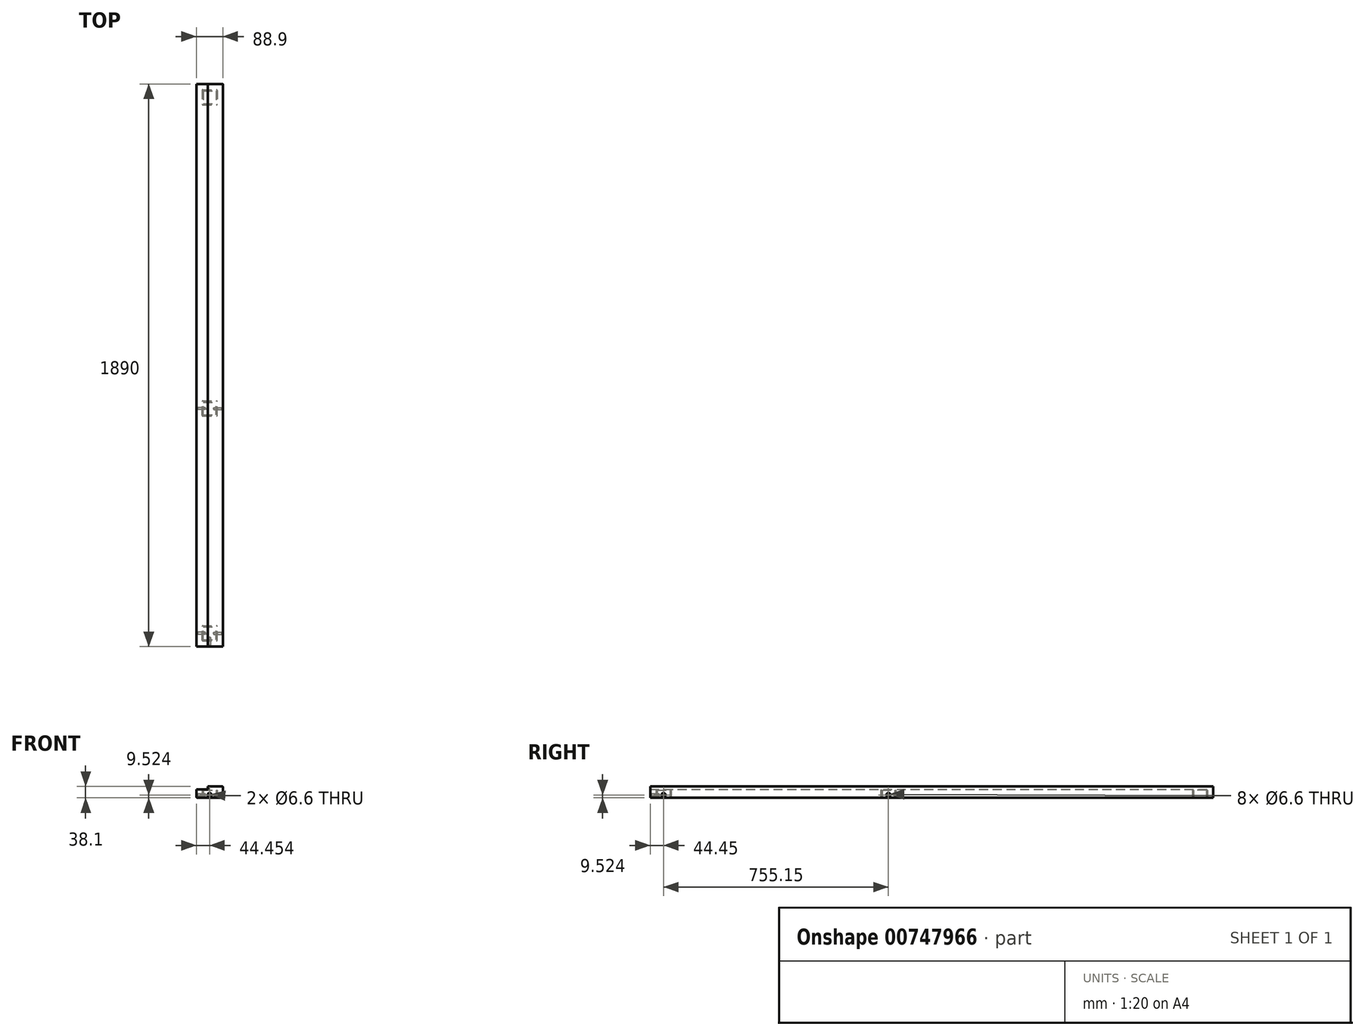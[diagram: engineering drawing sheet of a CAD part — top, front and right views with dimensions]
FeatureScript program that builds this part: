
annotation { "Feature Type Name" : "Feature", "Feature Type Description" : "" }
export const myFeature = defineFeature(function(context is Context, id is Id, definition is map)
    precondition{}
    {
        {
            var Q0;
            Q0=qCreatedBy(makeId("Front.planeOp"),FACE);
            var sketch = newSketch(context, id + "F0", { "sketchPlane" : qUnion([Q0])});
            skLineSegment(sketch, "E0.bottom", {"start": v(-21.3, 49.02) * mm, "end": v(26.5, 49.02) * mm});
            skLineSegment(sketch, "E0.top", {"start": v(-56.4, 10.92) * mm, "end": v(26.5, 10.92) * mm});
            skLineSegment(sketch, "E0.left", {"start": v(-59.4, 39.5) * mm, "end": v(-59.4, 13.92) * mm});
            skLineSegment(sketch, "E0.right", {"start": v(29.5, 46.02) * mm, "end": v(29.5, 13.92) * mm});
            skPoint(sketch, "E1.visualSharp", {"position": v(-59.4, 49.02) * mm});
            skPoint(sketch, "E2.visualSharp", {"position": v(-59.4, 10.92) * mm});
            skArc(sketch, "E2.filletArc", {"start": v(-59.4, 13.92) * mm, "mid": v(-58.52, 11.8) * mm, "end": v(-56.4, 10.92) * mm});
            skPoint(sketch, "E3.visualSharp", {"position": v(29.5, 49.02) * mm});
            skArc(sketch, "E3.filletArc", {"start": v(29.5, 46.02) * mm, "mid": v(28.63, 48.14) * mm, "end": v(26.5, 49.02) * mm});
            skPoint(sketch, "E4.visualSharp", {"position": v(29.5, 10.92) * mm});
            skArc(sketch, "E4.filletArc", {"start": v(26.5, 10.92) * mm, "mid": v(28.63, 11.8) * mm, "end": v(29.5, 13.92) * mm});
            skLineSegment(sketch, "E5", {"start": v(-21.3, 49.02) * mm, "end": v(-21.3, 39.5) * mm});
            skLineSegment(sketch, "E6", {"start": v(-21.3, 39.5) * mm, "end": v(-59.4, 39.5) * mm});
            skSolve(sketch);
        }
        {
            var Q0;
            Q0=makeQuery(id+"F0.imprint","IMPRINT",FACE,{"disambiguationData":[TD([[makeQuery(id+"F0.imprint","IMPRINT",EDGE,{"derivedFrom":sQuery(id+"F0.wireOp",EDGE,"E0.bottom")}),-1.0]])]});
            extrude(context, id + "F1", {"entities" : qUnion([Q0]), "depth" : 1890 * mm, "offsetDistance" : 25 * mm});
        }
        {
            var Q0;
            Q0=makeQuery(id+"F1.opExtrude","SWEPT_EDGE",EDGE,{"disambiguationData":[OSD([sQuery(id+"F0.wireOp",EDGE,"E0.bottom"),sQuery(id+"F0.wireOp",EDGE,"E3.filletArc")])]});
            cPoint(context, id + "F2", {"entities" : qUnion([Q0]), "parameter" : 0.5});
        }
        {
            var Q0;
            Q0=makeQuery(id+"F1.opExtrude","SWEPT_EDGE",EDGE,{"disambiguationData":[OSD([sQuery(id+"F0.wireOp",EDGE,"E0.left"),sQuery(id+"F0.wireOp",EDGE,"E2.filletArc")])]});
            cPoint(context, id + "F3", {"entities" : qUnion([Q0]), "parameter" : 0.5});
        }
        {
            var Q0;
            Q0=makeQuery(id+"F1.opExtrude","SWEPT_EDGE",EDGE,{"disambiguationData":[OSD([sQuery(id+"F0.wireOp",EDGE,"E5"),sQuery(id+"F0.wireOp",EDGE,"E6")])]});
            cPoint(context, id + "F4", {"entities" : qUnion([Q0]), "parameter" : 0.5});
        }
        {
            var Q0;
            Q0 = qCreatedBy(id + "F2" ,VERTEX);
            var Q1;
            Q1 = qCreatedBy(id + "F3" ,VERTEX);
            var Q2;
            Q2 = qCreatedBy(id + "F4" ,VERTEX);
            cPlane(context, id + "F5", {"entities" : qUnion([Q0, Q1, Q2]), "cplaneType" : CPlaneType.THREE_POINT, "offset" : 25 * mm, "width" : 150 * mm, "height" : 150 * mm});
        }
        {
            var Q0;
            Q0=makeQuery(id+"F1.opExtrude","SWEPT_FACE",FACE,{"disambiguationData":[OSD([sQuery(id+"F0.wireOp",EDGE,"E0.top")])]});
            var sketch = newSketch(context, id + "F6", { "sketchPlane" : qUnion([Q0])});
            skLineSegment(sketch, "E7.bottom", {"start": v(-37.85, 1870.95) * mm, "end": v(7.95, 1870.95) * mm});
            skLineSegment(sketch, "E7.top", {"start": v(-37.85, 1820.15) * mm, "end": v(7.95, 1820.15) * mm});
            skLineSegment(sketch, "E7.left", {"start": v(-40.35, 1868.45) * mm, "end": v(-40.35, 1822.65) * mm});
            skLineSegment(sketch, "E7.right", {"start": v(10.45, 1868.45) * mm, "end": v(10.45, 1822.65) * mm});
            skPoint(sketch, "E8.visualSharp", {"position": v(-40.35, 1870.95) * mm});
            skArc(sketch, "E8.filletArc", {"start": v(-37.85, 1870.95) * mm, "mid": v(-39.61, 1870.22) * mm, "end": v(-40.35, 1868.45) * mm});
            skPoint(sketch, "E9.visualSharp", {"position": v(-40.35, 1820.15) * mm});
            skArc(sketch, "E9.filletArc", {"start": v(-40.35, 1822.65) * mm, "mid": v(-39.61, 1820.88) * mm, "end": v(-37.85, 1820.15) * mm});
            skPoint(sketch, "E10.visualSharp", {"position": v(10.45, 1820.15) * mm});
            skArc(sketch, "E10.filletArc", {"start": v(7.95, 1820.15) * mm, "mid": v(9.72, 1820.88) * mm, "end": v(10.45, 1822.65) * mm});
            skPoint(sketch, "E11.visualSharp", {"position": v(10.45, 1870.95) * mm});
            skArc(sketch, "E11.filletArc", {"start": v(10.45, 1868.45) * mm, "mid": v(9.72, 1870.22) * mm, "end": v(7.95, 1870.95) * mm});
            skLineSegment(sketch, "E12.1", {"start": v(-36.35, 1866.95) * mm, "end": v(-36.35, 1824.15) * mm});
            skLineSegment(sketch, "E12.2", {"start": v(-36.35, 1866.95) * mm, "end": v(6.45, 1866.95) * mm});
            skLineSegment(sketch, "E12.5", {"start": v(6.45, 1866.95) * mm, "end": v(6.45, 1824.15) * mm});
            skLineSegment(sketch, "E12.7", {"start": v(-36.35, 1824.15) * mm, "end": v(6.45, 1824.15) * mm});
            skLineSegment(sketch, "E13", {"start": v(10.45, 1870.95) * mm, "end": v(-40.35, 1820.15) * mm, "construction": true});
            skLineSegment(sketch, "E14.0", {"start": v(-56.4, 1890) * mm, "end": v(26.5, 1890) * mm});
            skPoint(sketch, "E15", {"position": v(-14.95, 1845.55) * mm});
            skPoint(sketch, "E16", {"position": v(-14.95, 1890) * mm});
            skLineSegment(sketch, "E17", {"start": v(-56.4, 945) * mm, "end": v(26.5, 945) * mm, "construction": true});
            skLineSegment(sketch, "E18.bottom", {"start": v(-37.85, 1115.8) * mm, "end": v(7.95, 1115.8) * mm});
            skLineSegment(sketch, "E18.top", {"start": v(-37.85, 1065) * mm, "end": v(7.95, 1065) * mm});
            skLineSegment(sketch, "E18.left", {"start": v(-40.35, 1113.3) * mm, "end": v(-40.35, 1067.5) * mm});
            skLineSegment(sketch, "E18.right", {"start": v(10.45, 1113.3) * mm, "end": v(10.45, 1067.5) * mm});
            skPoint(sketch, "E19.visualSharp", {"position": v(-40.35, 1115.8) * mm});
            skArc(sketch, "E19.filletArc", {"start": v(-37.85, 1115.8) * mm, "mid": v(-39.61, 1115.07) * mm, "end": v(-40.35, 1113.3) * mm});
            skPoint(sketch, "E20.visualSharp", {"position": v(-40.35, 1065) * mm});
            skArc(sketch, "E20.filletArc", {"start": v(-40.35, 1067.5) * mm, "mid": v(-39.61, 1065.73) * mm, "end": v(-37.85, 1065) * mm});
            skPoint(sketch, "E21.visualSharp", {"position": v(10.45, 1065) * mm});
            skArc(sketch, "E21.filletArc", {"start": v(7.95, 1065) * mm, "mid": v(9.72, 1065.73) * mm, "end": v(10.45, 1067.5) * mm});
            skPoint(sketch, "E22.visualSharp", {"position": v(10.45, 1115.8) * mm});
            skArc(sketch, "E22.filletArc", {"start": v(10.45, 1113.3) * mm, "mid": v(9.72, 1115.07) * mm, "end": v(7.95, 1115.8) * mm});
            skLineSegment(sketch, "E23.1", {"start": v(-36.35, 1111.8) * mm, "end": v(-36.35, 1069) * mm});
            skLineSegment(sketch, "E23.2", {"start": v(-36.35, 1111.8) * mm, "end": v(6.45, 1111.8) * mm});
            skLineSegment(sketch, "E23.5", {"start": v(6.45, 1111.8) * mm, "end": v(6.45, 1069) * mm});
            skLineSegment(sketch, "E23.7", {"start": v(-36.35, 1069) * mm, "end": v(6.45, 1069) * mm});
            skLineSegment(sketch, "E24", {"start": v(10.45, 1115.8) * mm, "end": v(-40.35, 1065) * mm, "construction": true});
            skPoint(sketch, "E25", {"position": v(-14.95, 1090.4) * mm});
            skPoint(sketch, "E26", {"position": v(-14.95, 945) * mm});
            skLineSegment(sketch, "E27.MirrorCS", {"start": v(-36.35, 23.05) * mm, "end": v(-36.35, 65.85) * mm});
            skArc(sketch, "E28.MirrorCS", {"start": v(7.95, 69.85) * mm, "mid": v(9.72, 69.12) * mm, "end": v(10.45, 67.35) * mm});
            skArc(sketch, "E29.MirrorCS", {"start": v(10.45, 21.55) * mm, "mid": v(9.72, 19.78) * mm, "end": v(7.95, 19.05) * mm});
            skArc(sketch, "E30.MirrorCS", {"start": v(-37.85, 19.05) * mm, "mid": v(-39.61, 19.78) * mm, "end": v(-40.35, 21.55) * mm});
            skLineSegment(sketch, "E31.MirrorCS", {"start": v(-36.35, 23.05) * mm, "end": v(6.45, 23.05) * mm});
            skLineSegment(sketch, "E32.MirrorCS", {"start": v(-36.35, 65.85) * mm, "end": v(6.45, 65.85) * mm});
            skLineSegment(sketch, "E33.MirrorCS", {"start": v(-37.85, 69.85) * mm, "end": v(7.95, 69.85) * mm});
            skLineSegment(sketch, "E34.MirrorCS", {"start": v(6.45, 23.05) * mm, "end": v(6.45, 65.85) * mm});
            skLineSegment(sketch, "E35.MirrorCS", {"start": v(-40.35, 21.55) * mm, "end": v(-40.35, 67.35) * mm});
            skLineSegment(sketch, "E36.MirrorCS", {"start": v(-56.4, 0) * mm, "end": v(26.5, 0) * mm});
            skArc(sketch, "E37.MirrorCS", {"start": v(-40.35, 67.35) * mm, "mid": v(-39.61, 69.12) * mm, "end": v(-37.85, 69.85) * mm});
            skLineSegment(sketch, "E38.MirrorCS", {"start": v(-37.85, 19.05) * mm, "end": v(7.95, 19.05) * mm});
            skLineSegment(sketch, "E39.MirrorCS", {"start": v(10.45, 21.55) * mm, "end": v(10.45, 67.35) * mm});
            skLineSegment(sketch, "E40.MirrorCS", {"start": v(10.45, 19.05) * mm, "end": v(-40.35, 69.85) * mm, "construction": true});
            skPoint(sketch, "E41.MirrorP", {"position": v(-14.95, 44.45) * mm});
            skPoint(sketch, "E42.MirrorP", {"position": v(-14.95, 0) * mm});
            skPoint(sketch, "E43.MirrorP", {"position": v(-40.35, 19.05) * mm});
            skPoint(sketch, "E44.MirrorP", {"position": v(-40.35, 69.85) * mm});
            skPoint(sketch, "E45.MirrorP", {"position": v(10.45, 19.05) * mm});
            skPoint(sketch, "E46.MirrorP", {"position": v(10.45, 69.85) * mm});
            skSolve(sketch);
        }
        {
            var Q0;
            Q0 = qSketchRegion(id + "F6", true);
            extrude(context, id + "F7", {"entities" : qUnion([Q0]), "operationType" : NewBodyOperationType.REMOVE, "oppositeDirection" : true, "depth" : 25 * mm - 3 / 203.2 * mm, "offsetDistance" : 25 * mm});
        }
        {
            var Q0;
            Q0=makeQuery(id+"F1.opExtrude","CAP_FACE",FACE,{"disambiguationData":[OSD([sQuery(id+"F0.wireOp",EDGE,"E0.bottom"),sQuery(id+"F0.wireOp",EDGE,"E0.top"),sQuery(id+"F0.wireOp",EDGE,"E0.left"),sQuery(id+"F0.wireOp",EDGE,"E0.right"),sQuery(id+"F0.wireOp",EDGE,"E2.filletArc"),sQuery(id+"F0.wireOp",EDGE,"E3.filletArc"),sQuery(id+"F0.wireOp",EDGE,"E4.filletArc"),sQuery(id+"F0.wireOp",EDGE,"E5"),sQuery(id+"F0.wireOp",EDGE,"E6")])],"isStart":false});
            var sketch = newSketch(context, id + "F8", { "sketchPlane" : qUnion([Q0])});
            skLineSegment(sketch, "E47.0", {"start": v(-37.85, 26.4) * mm, "end": v(7.95, 26.4) * mm, "construction": true});
            skPoint(sketch, "E48", {"position": v(-14.95, 26.4) * mm});
            skPoint(sketch, "E49", {"position": v(-14.95, 20.44) * mm});
            skSolve(sketch);
        }
        {
            var Q0;
            Q0=sQuery(id+"F8.wireOp",VERTEX,"E49");
            var Q1;
            Q1=makeQuery(id+"F1.opExtrude","SWEPT_BODY",BODY,{"disambiguationData":[OSD([sQuery(id+"F0.wireOp",EDGE,"E0.bottom"),sQuery(id+"F0.wireOp",EDGE,"E0.top"),sQuery(id+"F0.wireOp",EDGE,"E0.left"),sQuery(id+"F0.wireOp",EDGE,"E0.right"),sQuery(id+"F0.wireOp",EDGE,"E2.filletArc"),sQuery(id+"F0.wireOp",EDGE,"E3.filletArc"),sQuery(id+"F0.wireOp",EDGE,"E4.filletArc"),sQuery(id+"F0.wireOp",EDGE,"E5"),sQuery(id+"F0.wireOp",EDGE,"E6")])]});
            hole(context, id + "F9", {"style" : HoleStyle.C_SINK, "endStyle" : HoleEndStyle.BLIND, "standardTappedOrClearance" : lookupTablePath({ "fit" : "Normal", "standard" : "ISO", "size" : "M6", "type" : "Clearance" }), "standardBlindInLast" : lookupTablePath({ "fit" : "Standard", "standard" : "ISO", "size" : "M6", "type" : "Clearance" }), "holeDiameter" : 6.6 * mm, "cSinkDiameter" : 13.44 * mm, "cSinkAngle" : 90 * degree, "majorDiameter" : 6 * mm, "holeDepth" : 30 * mm, "isTappedThrough" : true, "tappedDepth" : 12 * mm, "tapClearance" : 3, "startFromSketch" : true, "locations" : qUnion([Q0]), "scope" : qUnion([Q1])});
        }
        {
            var Q0;
            Q0=makeQuery(id+"F1.opExtrude","SWEPT_FACE",FACE,{"disambiguationData":[OSD([sQuery(id+"F0.wireOp",EDGE,"E0.right")])]});
            var sketch = newSketch(context, id + "F10", { "sketchPlane" : qUnion([Q0])});
            skLineSegment(sketch, "E50.0", {"start": v(-1868.45, 26.4) * mm, "end": v(-1822.65, 26.4) * mm, "construction": true});
            skPoint(sketch, "E51", {"position": v(-1845.55, 20.44) * mm});
            skPoint(sketch, "E51.positionSnap0", {"position": v(-1845.55, 26.4) * mm});
            skLineSegment(sketch, "E52.0", {"start": v(-1113.3, 26.4) * mm, "end": v(-1067.5, 26.4) * mm, "construction": true});
            skPoint(sketch, "E53", {"position": v(-1090.4, 20.44) * mm});
            skPoint(sketch, "E53.positionSnap0", {"position": v(-1090.4, 26.4) * mm});
            skSolve(sketch);
        }
        {
            var Q0;
            Q0=sQuery(id+"F10.wireOp",VERTEX,"E51");
            var Q1;
            Q1=makeQuery(id+"F1.opExtrude","SWEPT_BODY",BODY,{"disambiguationData":[OSD([sQuery(id+"F0.wireOp",EDGE,"E0.bottom"),sQuery(id+"F0.wireOp",EDGE,"E0.top"),sQuery(id+"F0.wireOp",EDGE,"E0.left"),sQuery(id+"F0.wireOp",EDGE,"E0.right"),sQuery(id+"F0.wireOp",EDGE,"E2.filletArc"),sQuery(id+"F0.wireOp",EDGE,"E3.filletArc"),sQuery(id+"F0.wireOp",EDGE,"E4.filletArc"),sQuery(id+"F0.wireOp",EDGE,"E5"),sQuery(id+"F0.wireOp",EDGE,"E6")])]});
            hole(context, id + "F11", {"style" : HoleStyle.C_SINK, "endStyle" : HoleEndStyle.BLIND, "standardTappedOrClearance" : lookupTablePath({ "fit" : "Normal", "standard" : "ISO", "size" : "M6", "type" : "Clearance" }), "standardBlindInLast" : lookupTablePath({ "fit" : "Standard", "standard" : "ISO", "size" : "M6", "type" : "Clearance" }), "holeDiameter" : 6.6 * mm, "cSinkDiameter" : 13.44 * mm, "cSinkAngle" : 90 * degree, "majorDiameter" : 6 * mm, "holeDepth" : 30 * mm, "isTappedThrough" : true, "tappedDepth" : 27 * mm, "tapClearance" : 3, "startFromSketch" : true, "locations" : qUnion([Q0]), "scope" : qUnion([Q1])});
        }
        {
            var Q0;
            Q0=makeQuery(id+"F1.opExtrude","SWEPT_FACE",FACE,{"disambiguationData":[OSD([sQuery(id+"F0.wireOp",EDGE,"E0.left")])]});
            var sketch = newSketch(context, id + "F12", { "sketchPlane" : qUnion([Q0])});
            skLineSegment(sketch, "E54.0", {"start": v(1868.45, 26.4) * mm, "end": v(1822.65, 26.4) * mm, "construction": true});
            skPoint(sketch, "E55", {"position": v(1845.55, 20.44) * mm});
            skPoint(sketch, "E55.positionSnap0", {"position": v(1845.55, 26.4) * mm});
            skLineSegment(sketch, "E56.0", {"start": v(1113.3, 26.4) * mm, "end": v(1067.5, 26.4) * mm, "construction": true});
            skPoint(sketch, "E57", {"position": v(1090.4, 20.44) * mm});
            skPoint(sketch, "E57.positionSnap0", {"position": v(1090.4, 26.4) * mm});
            skSolve(sketch);
        }
        {
            var Q0;
            Q0=sQuery(id+"F12.wireOp",VERTEX,"E55");
            var Q1;
            Q1=makeQuery(id+"F1.opExtrude","SWEPT_BODY",BODY,{"disambiguationData":[OSD([sQuery(id+"F0.wireOp",EDGE,"E0.bottom"),sQuery(id+"F0.wireOp",EDGE,"E0.top"),sQuery(id+"F0.wireOp",EDGE,"E0.left"),sQuery(id+"F0.wireOp",EDGE,"E0.right"),sQuery(id+"F0.wireOp",EDGE,"E2.filletArc"),sQuery(id+"F0.wireOp",EDGE,"E3.filletArc"),sQuery(id+"F0.wireOp",EDGE,"E4.filletArc"),sQuery(id+"F0.wireOp",EDGE,"E5"),sQuery(id+"F0.wireOp",EDGE,"E6")])]});
            hole(context, id + "F13", {"style" : HoleStyle.C_SINK, "endStyle" : HoleEndStyle.BLIND, "standardTappedOrClearance" : lookupTablePath({ "fit" : "Normal", "standard" : "ISO", "size" : "M6", "type" : "Clearance" }), "standardBlindInLast" : lookupTablePath({ "fit" : "Standard", "standard" : "ISO", "size" : "M6", "type" : "Clearance" }), "holeDiameter" : 6.6 * mm, "cSinkDiameter" : 13.44 * mm, "cSinkAngle" : 90 * degree, "majorDiameter" : 5 * mm, "holeDepth" : 30 * mm, "isTappedThrough" : true, "tappedDepth" : 12 * mm, "tapClearance" : 3, "startFromSketch" : true, "locations" : qUnion([Q0]), "scope" : qUnion([Q1])});
        }
        {
            var Q0;
            Q0=sQuery(id+"F12.wireOp",VERTEX,"E57");
            var Q1;
            Q1=makeQuery(id+"F1.opExtrude","SWEPT_BODY",BODY,{"disambiguationData":[OSD([sQuery(id+"F0.wireOp",EDGE,"E0.bottom"),sQuery(id+"F0.wireOp",EDGE,"E0.top"),sQuery(id+"F0.wireOp",EDGE,"E0.left"),sQuery(id+"F0.wireOp",EDGE,"E0.right"),sQuery(id+"F0.wireOp",EDGE,"E2.filletArc"),sQuery(id+"F0.wireOp",EDGE,"E3.filletArc"),sQuery(id+"F0.wireOp",EDGE,"E4.filletArc"),sQuery(id+"F0.wireOp",EDGE,"E5"),sQuery(id+"F0.wireOp",EDGE,"E6")])]});
            hole(context, id + "F14", {"style" : HoleStyle.C_SINK, "endStyle" : HoleEndStyle.BLIND, "standardTappedOrClearance" : lookupTablePath({ "fit" : "Normal", "standard" : "ISO", "size" : "M6", "type" : "Clearance" }), "standardBlindInLast" : lookupTablePath({ "fit" : "Standard", "standard" : "ISO", "size" : "M6", "type" : "Clearance" }), "holeDiameter" : 6.6 * mm, "cSinkDiameter" : 13.44 * mm, "cSinkAngle" : 90 * degree, "majorDiameter" : 5 * mm, "holeDepth" : 30 * mm, "isTappedThrough" : true, "tappedDepth" : 12 * mm, "tapClearance" : 3, "startFromSketch" : true, "locations" : qUnion([Q0]), "scope" : qUnion([Q1])});
        }
        {
            var Q0;
            Q0=sQuery(id+"F10.wireOp",VERTEX,"E53");
            var Q1;
            Q1=makeQuery(id+"F1.opExtrude","SWEPT_BODY",BODY,{"disambiguationData":[OSD([sQuery(id+"F0.wireOp",EDGE,"E0.bottom"),sQuery(id+"F0.wireOp",EDGE,"E0.top"),sQuery(id+"F0.wireOp",EDGE,"E0.left"),sQuery(id+"F0.wireOp",EDGE,"E0.right"),sQuery(id+"F0.wireOp",EDGE,"E2.filletArc"),sQuery(id+"F0.wireOp",EDGE,"E3.filletArc"),sQuery(id+"F0.wireOp",EDGE,"E4.filletArc"),sQuery(id+"F0.wireOp",EDGE,"E5"),sQuery(id+"F0.wireOp",EDGE,"E6")])]});
            hole(context, id + "F15", {"style" : HoleStyle.C_SINK, "endStyle" : HoleEndStyle.BLIND, "standardTappedOrClearance" : lookupTablePath({ "fit" : "Normal", "standard" : "ISO", "size" : "M6", "type" : "Clearance" }), "standardBlindInLast" : lookupTablePath({ "fit" : "Standard", "standard" : "ISO", "size" : "M6", "type" : "Clearance" }), "holeDiameter" : 6.6 * mm, "cSinkDiameter" : 13.44 * mm, "cSinkAngle" : 90 * degree, "majorDiameter" : 5 * mm, "holeDepth" : 30 * mm, "isTappedThrough" : true, "tappedDepth" : 12 * mm, "tapClearance" : 3, "startFromSketch" : true, "locations" : qUnion([Q0]), "scope" : qUnion([Q1])});
        }
    });
